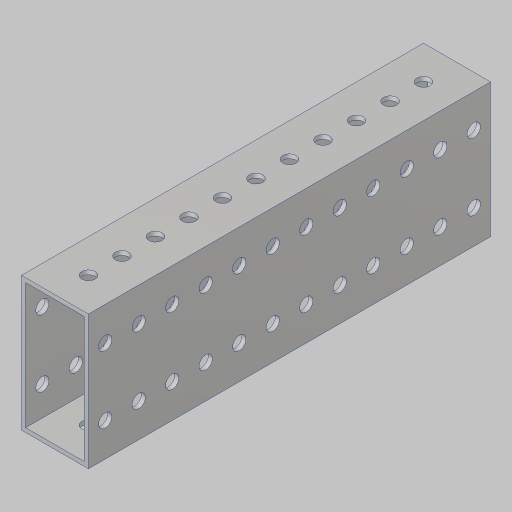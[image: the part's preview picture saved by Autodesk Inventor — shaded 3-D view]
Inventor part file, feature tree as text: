
AUTODESK INVENTOR PART (.ipt)
format: ipt  version: 2023.5 (Build 275446000, 446)  size: 209,408 bytes
history: native  units: in
note: dims shown in document units (in); Inventor stores cm internally (conversion verified against a paired STEP export)
features: hole x2, sketch x2, projected_geometry x2, extrude x1
ambient origin geometry x8: Origin, YZ Plane, XZ Plane, XY Plane, X Axis, Y Axis, Z Axis, Center Point
bodies: Solid1 (feature_tree)
feature tree (7):
  extrude  "Extrusion1"  Depth=0.5in
  hole  "Hole1"  [1 undecoded]
  hole  "Hole2"  [1 undecoded]
  sketch  "Sketch2"  dims[d4=0.0in d5=0.5in]
  projected_geometry  "Projected Loop1"
  sketch  "Sketch3"  dims[d6=4.3307in d8=0.5in d9=0.3937in d11=1.0in d13=0.201in d14=0.75in d15=0.375in d16=0.19in d17=0.5635in d18=1.0in d19=0.8108in d20=1.0in d21=0.25in d22=4.7244in d24=0.5in d25=0.3937in d27=1.0in d29=0.201in d30=0.75in d31=0.375in d32=0.25in d33=0.5635in d34=1.0in d35=0.8108in]
  projected_geometry  "Projected Loop2"
note: 2 required parameter values undecoded (feature->parameter linkage not recoverable at this tier; creation-order binding heuristic only, values carry confidence <= 0.55)
